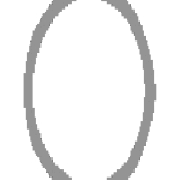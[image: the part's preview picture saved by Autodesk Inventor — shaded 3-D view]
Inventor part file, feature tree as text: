
AUTODESK INVENTOR PART (.ipt)
format: ipt  version: 2021 (Build 250183000, 183)  size: 110,080 bytes
history: native  units: in
note: dims shown in document units (in); Inventor stores cm internally (conversion verified against a paired STEP export)
features: other x4, sketch x3, plane x1
ambient origin geometry x8: Origin, YZ Plane, XZ Plane, XY Plane, X Axis, Y Axis, Z Axis, Center Point
bodies: Solid1 (feature_tree), Body (feature_tree)
feature tree (8):
  other  "Driven Length"
  other  "Frame Generator"
  other  "Start Plane"
  other  "End Plane"
  sketch  "Sketch"  dims[d2=8.0898in d4=-0.0in d5=8.0898in d6=0.12in d7=0.0in d8=90.0deg d9=8.0898in]
  sketch  "Sketch2"  dims[d0=1.0in]
  plane  "Work Plane3"
  sketch  "Sketch3"  dims[d1=0.065in]
